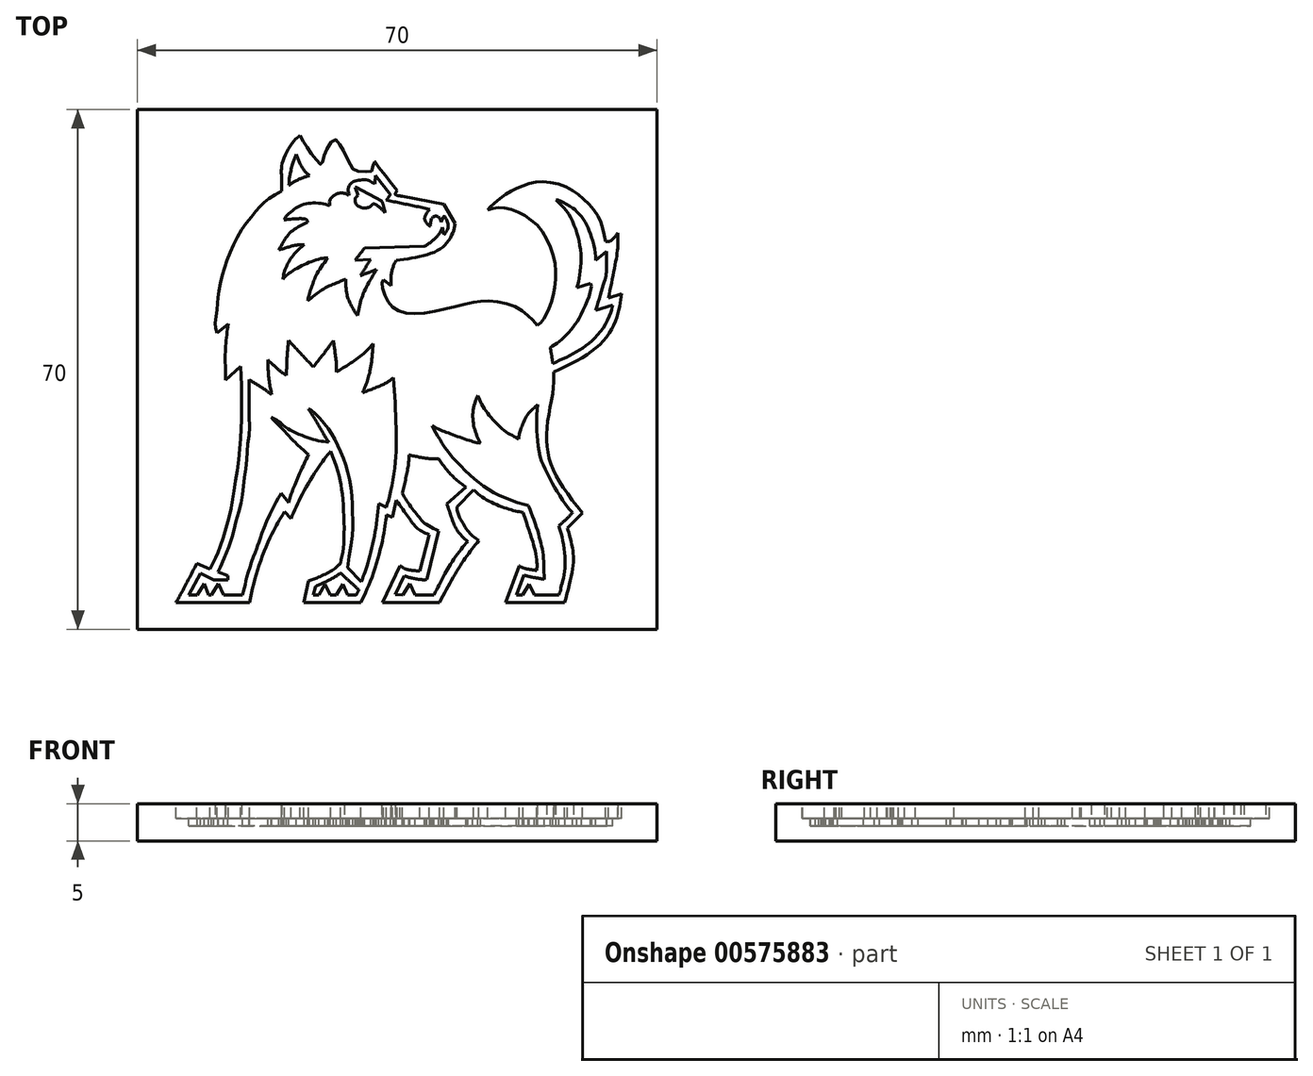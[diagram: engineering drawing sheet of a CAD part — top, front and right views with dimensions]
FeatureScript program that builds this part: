
annotation { "Feature Type Name" : "Feature", "Feature Type Description" : "" }
export const myFeature = defineFeature(function(context is Context, id is Id, definition is map)
    precondition{}
    {
        {
            var Q0;
            Q0=qCreatedBy(makeId("Top.planeOp"),FACE);
            var sketch = newSketch(context, id + "F0", { "sketchPlane" : qUnion([Q0])});
            skLineSegment(sketch, "E0.bottom", {"start": v(0, 0) * mm, "end": v(70, 0) * mm});
            skLineSegment(sketch, "E0.top", {"start": v(0, 70) * mm, "end": v(70, 70) * mm});
            skLineSegment(sketch, "E0.left", {"start": v(0, 0) * mm, "end": v(0, 70) * mm});
            skLineSegment(sketch, "E0.right", {"start": v(70, 0) * mm, "end": v(70, 70) * mm});
            skSolve(sketch);
        }
        {
            var Q0;
            Q0 = qSketchRegion(id + "F0", true);
            extrude(context, id + "F1", {"entities" : qUnion([Q0]), "depth" : 5 * mm, "offsetDistance" : 25 * mm});
        }
        {
            var Q0;
            Q0=makeQuery(id+"F1.opExtrude","CAP_FACE",FACE,{"disambiguationData":[OSD([sQuery(id+"F0.wireOp",EDGE,"E0.bottom"),sQuery(id+"F0.wireOp",EDGE,"E0.top"),sQuery(id+"F0.wireOp",EDGE,"E0.left"),sQuery(id+"F0.wireOp",EDGE,"E0.right")])],"isStart":false});
            var sketch = newSketch(context, id + "F2", { "sketchPlane" : qUnion([Q0])});
            skLineSegment(sketch, "E1", {"start": v(2.5, 2.5) * mm, "end": v(0, 2.5) * mm});
            skLineSegment(sketch, "E2", {"start": v(67.5, 67.5) * mm, "end": v(67.5, 70) * mm});
            skFitSpline(sketch, "E3", {"points": [v(21.94, 66.5) * mm, v(22.53, 65.47) * mm, v(23.24, 64.36) * mm, v(24.27, 63.03) * mm, v(24.75, 62.63) * mm, v(24.92, 62.83) * mm, v(25.12, 63.73) * mm, v(25.77, 65.15) * mm, v(26.63, 65.97) * mm, v(27.13, 65.54) * mm, v(27.88, 64.24) * mm, v(29.14, 61.88) * mm, v(29.98, 61.7) * mm, v(31.5, 61.67) * mm, v(31.61, 61.88) * mm, v(31.95, 63.03) * mm, v(32.14, 62.8) * mm, v(33.59, 60.92) * mm, v(35, 59.1) * mm], "startDerivative": vector(10.08, -18.23) * mm, "endDerivative": vector(16.66, -21.81) * mm});
            skFitSpline(sketch, "E4", {"points": [v(35, 59.1) * mm, v(34.77, 58.58) * mm, v(35.68, 58.34) * mm], "startDerivative": vector(-1, -1.38) * mm, "endDerivative": vector(2.24, -0.2) * mm});
            skFitSpline(sketch, "E5", {"points": [v(35.68, 58.34) * mm, v(41.28, 57.23) * mm], "startDerivative": vector(5.6, -1.11) * mm, "endDerivative": vector(5.6, -1.11) * mm});
            skFitSpline(sketch, "E6", {"points": [v(41.28, 57.23) * mm, v(42.8, 54.64) * mm], "startDerivative": vector(1.51, -2.6) * mm, "endDerivative": vector(1.51, -2.6) * mm});
            skFitSpline(sketch, "E7", {"points": [v(42.8, 54.64) * mm, v(42.56, 53.6) * mm, v(41.81, 52.2) * mm, v(40.47, 51.03) * mm, v(37.83, 50.17) * mm, v(34.89, 49.7) * mm], "startDerivative": vector(-1.1, -6.76) * mm, "endDerivative": vector(-11.91, -1.57) * mm});
            skFitSpline(sketch, "E8", {"points": [v(34.89, 49.7) * mm, v(34.47, 48.87) * mm, v(34.17, 47.56) * mm, v(34.2, 46.28) * mm], "startDerivative": vector(-1.48, -2.6) * mm, "endDerivative": vector(0.3, -3.62) * mm});
            skFitSpline(sketch, "E9", {"points": [v(34.2, 46.28) * mm, v(33.16, 47.08) * mm], "startDerivative": vector(-1.05, 0.8) * mm, "endDerivative": vector(-1.05, 0.8) * mm});
            skFitSpline(sketch, "E10", {"points": [v(33.16, 47.08) * mm, v(32.94, 46.66) * mm, v(33.34, 45) * mm, v(34.44, 43.36) * mm, v(36.65, 42.53) * mm, v(40.63, 42.94) * mm, v(44.7, 43.94) * mm, v(47.06, 44.24) * mm, v(50.35, 43.7) * mm, v(52.54, 42.35) * mm, v(53.84, 40.92) * mm], "startDerivative": vector(-6.38, -7.42) * mm, "endDerivative": vector(13.18, -16.1) * mm});
            skFitSpline(sketch, "E11", {"points": [v(53.84, 40.92) * mm, v(54.6, 41.6) * mm, v(55.27, 42.84) * mm, v(55.9, 44.58) * mm, v(56.34, 47.49) * mm, v(56.06, 50.23) * mm, v(54.6, 53.51) * mm, v(52.64, 55.43) * mm, v(50.35, 56.57) * mm, v(48.53, 56.8) * mm, v(47.19, 56.51) * mm], "startDerivative": vector(11.68, 8.6) * mm, "endDerivative": vector(-16.17, -4.46) * mm});
            skFitSpline(sketch, "E12", {"points": [v(47.19, 56.51) * mm, v(47.74, 57.1) * mm, v(49.46, 58.49) * mm, v(51.18, 59.46) * mm, v(53.06, 60.1) * mm, v(55.3, 60.25) * mm, v(58.13, 59.4) * mm, v(60, 58.07) * mm, v(61.73, 56.18) * mm, v(62.66, 54.16) * mm, v(63.05, 52.27) * mm], "startDerivative": vector(7.28, 8.52) * mm, "endDerivative": vector(3.26, -19.58) * mm});
            skFitSpline(sketch, "E13", {"points": [v(63.05, 52.27) * mm, v(63.65, 52.27) * mm, v(64.7, 53.35) * mm], "startDerivative": vector(1.5, -0.34) * mm, "endDerivative": vector(1.75, 2.31) * mm});
            skFitSpline(sketch, "E14", {"points": [v(64.7, 53.35) * mm, v(64.7, 51.32) * mm, v(63.43, 44.64) * mm], "startDerivative": vector(0.35, -4.94) * mm, "endDerivative": vector(-2.58, -11.82) * mm});
            skFitSpline(sketch, "E15", {"points": [v(63.43, 44.64) * mm, v(65.22, 45.2) * mm], "startDerivative": vector(1.79, 0.56) * mm, "endDerivative": vector(1.79, 0.56) * mm});
            skFitSpline(sketch, "E16", {"points": [v(65.22, 45.2) * mm, v(64.96, 43.49) * mm, v(64.13, 40.92) * mm, v(61.62, 37.75) * mm, v(56.08, 34.65) * mm], "startDerivative": vector(-1.16, -9.37) * mm, "endDerivative": vector(-18.65, -8.62) * mm});
            skFitSpline(sketch, "E17", {"points": [v(56.08, 34.65) * mm, v(56.08, 32.87) * mm, v(55.6, 29.96) * mm, v(55.14, 26.8) * mm, v(55.23, 24.22) * mm, v(55.84, 21.85) * mm, v(57.37, 19.08) * mm, v(59.93, 15.67) * mm], "startDerivative": vector(0.72, -14.91) * mm, "endDerivative": vector(15.62, -19.82) * mm});
            skFitSpline(sketch, "E18", {"points": [v(59.93, 15.67) * mm, v(57.93, 13.63) * mm], "startDerivative": vector(-2, -2.04) * mm, "endDerivative": vector(-2, -2.04) * mm});
            skFitSpline(sketch, "E19", {"points": [v(57.93, 13.63) * mm, v(58.26, 12.43) * mm, v(58.68, 10.46) * mm, v(58.61, 8.13) * mm, v(57.56, 3.57) * mm], "startDerivative": vector(1.74, -6.23) * mm, "endDerivative": vector(-3.71, -14.22) * mm});
            skFitSpline(sketch, "E20", {"points": [v(57.56, 3.57) * mm, v(49.62, 3.57) * mm], "startDerivative": vector(-7.94, 0) * mm, "endDerivative": vector(-7.94, 0) * mm});
            skFitSpline(sketch, "E21", {"points": [v(49.62, 3.57) * mm, v(51.43, 8.58) * mm], "startDerivative": vector(1.8, 5) * mm, "endDerivative": vector(1.8, 5) * mm});
            skFitSpline(sketch, "E22", {"points": [v(51.43, 8.58) * mm, v(52.01, 8.25) * mm, v(53.8, 7.92) * mm], "startDerivative": vector(1.3, -0.93) * mm, "endDerivative": vector(3.28, -0.42) * mm});
            skFitSpline(sketch, "E23", {"points": [v(53.8, 7.92) * mm, v(53.8, 9.35) * mm, v(53.21, 11.98) * mm, v(52.67, 13.6) * mm, v(51.94, 15.74) * mm], "startDerivative": vector(0.45, 6.08) * mm, "endDerivative": vector(-2.87, 8.51) * mm});
            skFitSpline(sketch, "E24", {"points": [v(51.94, 15.74) * mm, v(50.67, 16) * mm, v(48.8, 16.61) * mm, v(46.54, 17.76) * mm, v(45.32, 18.77) * mm], "startDerivative": vector(-5.8, 1.04) * mm, "endDerivative": vector(-4.65, 4.34) * mm});
            skFitSpline(sketch, "E25", {"points": [v(45.32, 18.77) * mm, v(43.04, 16.47) * mm], "startDerivative": vector(-2.28, -2.3) * mm, "endDerivative": vector(-2.28, -2.3) * mm});
            skFitSpline(sketch, "E26", {"points": [v(43.04, 16.47) * mm, v(43.23, 15.46) * mm, v(43.79, 14.38) * mm, v(44.78, 12.95) * mm, v(46, 11.96) * mm], "startDerivative": vector(0.53, -4.75) * mm, "endDerivative": vector(4.8, -3.28) * mm});
            skFitSpline(sketch, "E27", {"points": [v(46, 11.96) * mm, v(43.65, 8.81) * mm, v(40.7, 3.6) * mm], "startDerivative": vector(-5.23, -6.5) * mm, "endDerivative": vector(-5.37, -10.1) * mm});
            skFitSpline(sketch, "E28", {"points": [v(40.7, 3.6) * mm, v(33.04, 3.6) * mm], "startDerivative": vector(-7.66, 0) * mm, "endDerivative": vector(-7.66, 0) * mm});
            skFitSpline(sketch, "E29", {"points": [v(33.04, 3.6) * mm, v(35.41, 8.57) * mm], "startDerivative": vector(2.37, 4.98) * mm, "endDerivative": vector(2.37, 4.98) * mm});
            skFitSpline(sketch, "E30", {"points": [v(35.41, 8.57) * mm, v(36.16, 8.11) * mm, v(38.04, 7.86) * mm], "startDerivative": vector(1.6, -1.27) * mm, "endDerivative": vector(3.54, -0.23) * mm});
            skFitSpline(sketch, "E31", {"points": [v(38.04, 7.86) * mm, v(39.35, 12.73) * mm], "startDerivative": vector(1.3, 4.88) * mm, "endDerivative": vector(1.3, 4.88) * mm});
            skFitSpline(sketch, "E32", {"points": [v(39.35, 12.73) * mm, v(37.69, 13.62) * mm, v(36.78, 14.75) * mm, v(34.88, 17.36) * mm], "startDerivative": vector(-5.91, 2.6) * mm, "endDerivative": vector(-5.17, 6.96) * mm});
            skFitSpline(sketch, "E33", {"points": [v(34.88, 17.36) * mm, v(34.35, 15.07) * mm], "startDerivative": vector(-0.53, -2.3) * mm, "endDerivative": vector(-0.53, -2.3) * mm});
            skFitSpline(sketch, "E34", {"points": [v(34.35, 15.07) * mm, v(33.56, 15.42) * mm], "startDerivative": vector(-0.8, 0.36) * mm, "endDerivative": vector(-0.8, 0.36) * mm});
            skFitSpline(sketch, "E35", {"points": [v(33.56, 15.42) * mm, v(33.34, 13.76) * mm, v(32.7, 10.62) * mm, v(31.34, 6.32) * mm, v(30.09, 3.6) * mm], "startDerivative": vector(-0.98, -8.32) * mm, "endDerivative": vector(-5, -10.1) * mm});
            skFitSpline(sketch, "E36", {"points": [v(30.09, 3.6) * mm, v(22.41, 3.6) * mm], "startDerivative": vector(-7.67, 0) * mm, "endDerivative": vector(-7.67, 0) * mm});
            skFitSpline(sketch, "E37", {"points": [v(22.41, 3.6) * mm, v(23.08, 6.52) * mm], "startDerivative": vector(0.66, 2.92) * mm, "endDerivative": vector(0.66, 2.92) * mm});
            skFitSpline(sketch, "E38", {"points": [v(23.08, 6.52) * mm, v(24.52, 7.06) * mm, v(26.52, 8.13) * mm, v(27.35, 8.9) * mm], "startDerivative": vector(4.12, 1.43) * mm, "endDerivative": vector(2.47, 2.69) * mm});
            skFitSpline(sketch, "E39", {"points": [v(27.35, 8.9) * mm, v(27.72, 10.73) * mm, v(27.85, 13.89) * mm, v(27.64, 18) * mm, v(27.16, 20.72) * mm, v(26.06, 24) * mm], "startDerivative": vector(2.64, 10.97) * mm, "endDerivative": vector(-5.84, 15.89) * mm});
            skFitSpline(sketch, "E40", {"points": [v(26.06, 24) * mm, v(24.63, 22.16) * mm, v(22.18, 18.11) * mm, v(20.7, 14.9) * mm], "startDerivative": vector(-4.86, -5.86) * mm, "endDerivative": vector(-3.84, -9.06) * mm});
            skFitSpline(sketch, "E41", {"points": [v(20.7, 14.9) * mm, v(19.85, 15.86) * mm], "startDerivative": vector(-0.85, 0.97) * mm, "endDerivative": vector(-0.85, 0.97) * mm});
            skFitSpline(sketch, "E42", {"points": [v(19.85, 15.86) * mm, v(19, 14.48) * mm, v(18.31, 13.2) * mm, v(17.07, 10.41) * mm, v(15.88, 6.95) * mm, v(15.13, 3.6) * mm], "startDerivative": vector(-5.6, -8.96) * mm, "endDerivative": vector(-2.86, -14.46) * mm});
            skFitSpline(sketch, "E43", {"points": [v(15.13, 3.6) * mm, v(5.21, 3.6) * mm], "startDerivative": vector(-9.92, 0) * mm, "endDerivative": vector(-9.92, 0) * mm});
            skFitSpline(sketch, "E44", {"points": [v(5.21, 3.6) * mm, v(6.22, 5.4) * mm, v(8.02, 8.9) * mm], "startDerivative": vector(2.25, 3.92) * mm, "endDerivative": vector(3.3, 6.54) * mm});
            skFitSpline(sketch, "E45", {"points": [v(8.02, 8.9) * mm, v(9.78, 8.14) * mm], "startDerivative": vector(1.76, -0.75) * mm, "endDerivative": vector(1.76, -0.75) * mm});
            skFitSpline(sketch, "E46", {"points": [v(9.78, 8.14) * mm, v(10.57, 9.68) * mm, v(11.24, 11.34) * mm, v(12.48, 15.57) * mm, v(13.14, 19.24) * mm, v(13.8, 24.24) * mm, v(14.03, 28.47) * mm, v(14.06, 31.53) * mm, v(13.89, 35.42) * mm], "startDerivative": vector(9.35, 17.64) * mm, "endDerivative": vector(-1.76, 30.16) * mm});
            skFitSpline(sketch, "E47", {"points": [v(13.89, 35.42) * mm, v(11.87, 33.56) * mm], "startDerivative": vector(-2.02, -1.86) * mm, "endDerivative": vector(-2.02, -1.86) * mm});
            skFitSpline(sketch, "E48", {"points": [v(11.87, 33.56) * mm, v(11.87, 34.73) * mm, v(11.87, 37.75) * mm, v(12.27, 41.13) * mm], "startDerivative": vector(0.05, 4.42) * mm, "endDerivative": vector(1.28, 8.4) * mm});
            skFitSpline(sketch, "E49", {"points": [v(12.27, 41.13) * mm, v(10.75, 39.9) * mm], "startDerivative": vector(-1.52, -1.22) * mm, "endDerivative": vector(-1.52, -1.22) * mm});
            skFitSpline(sketch, "E50", {"points": [v(10.75, 39.9) * mm, v(10.5, 41.13) * mm, v(10.75, 43.28) * mm, v(10.92, 45.16) * mm, v(11.53, 48.02) * mm, v(12.63, 51.08) * mm, v(14.32, 54.2) * mm, v(16.1, 56.46) * mm, v(17.33, 57.7) * mm, v(19.42, 59.06) * mm], "startDerivative": vector(-4.25, 13.95) * mm, "endDerivative": vector(20.21, 12) * mm});
            skFitSpline(sketch, "E51", {"points": [v(19.42, 59.06) * mm, v(19.42, 60.87) * mm, v(19.42, 62) * mm, v(19.85, 63.74) * mm, v(21.14, 65.83) * mm, v(21.94, 66.5) * mm], "startDerivative": vector(0.09, 9.13) * mm, "endDerivative": vector(4.8, 3.22) * mm});
            skSolve(sketch);
        }
        {
            var Q0;
            Q0 = qSketchRegion(id + "F2", true);
            extrude(context, id + "F3", {"entities" : qUnion([Q0]), "operationType" : NewBodyOperationType.REMOVE, "oppositeDirection" : true, "depth" : 2 * mm, "offsetDistance" : 25 * mm});
        }
        {
            var Q0;
            Q0=makeQuery(id+"F3.boolean.opBoolean","COPY",FACE,{"derivedFrom":makeQuery(id+"F3.opExtrude","CAP_FACE",FACE,{"disambiguationData":[OSD([sQuery(id+"F2.wireOp",EDGE,"E3"),sQuery(id+"F2.wireOp",EDGE,"E4"),sQuery(id+"F2.wireOp",EDGE,"E5"),sQuery(id+"F2.wireOp",EDGE,"E6"),sQuery(id+"F2.wireOp",EDGE,"E7"),sQuery(id+"F2.wireOp",EDGE,"E8"),sQuery(id+"F2.wireOp",EDGE,"E9"),sQuery(id+"F2.wireOp",EDGE,"E10"),sQuery(id+"F2.wireOp",EDGE,"E11"),sQuery(id+"F2.wireOp",EDGE,"E12"),sQuery(id+"F2.wireOp",EDGE,"E13"),sQuery(id+"F2.wireOp",EDGE,"E14"),sQuery(id+"F2.wireOp",EDGE,"E15"),sQuery(id+"F2.wireOp",EDGE,"E16"),sQuery(id+"F2.wireOp",EDGE,"E17"),sQuery(id+"F2.wireOp",EDGE,"E18"),sQuery(id+"F2.wireOp",EDGE,"E19"),sQuery(id+"F2.wireOp",EDGE,"E20"),sQuery(id+"F2.wireOp",EDGE,"E21"),sQuery(id+"F2.wireOp",EDGE,"E22"),sQuery(id+"F2.wireOp",EDGE,"E23"),sQuery(id+"F2.wireOp",EDGE,"E24"),sQuery(id+"F2.wireOp",EDGE,"E25"),sQuery(id+"F2.wireOp",EDGE,"E26"),sQuery(id+"F2.wireOp",EDGE,"E27"),sQuery(id+"F2.wireOp",EDGE,"E28"),sQuery(id+"F2.wireOp",EDGE,"E29"),sQuery(id+"F2.wireOp",EDGE,"E30"),sQuery(id+"F2.wireOp",EDGE,"E31"),sQuery(id+"F2.wireOp",EDGE,"E32"),sQuery(id+"F2.wireOp",EDGE,"E33"),sQuery(id+"F2.wireOp",EDGE,"E34"),sQuery(id+"F2.wireOp",EDGE,"E35"),sQuery(id+"F2.wireOp",EDGE,"E36"),sQuery(id+"F2.wireOp",EDGE,"E37"),sQuery(id+"F2.wireOp",EDGE,"E38"),sQuery(id+"F2.wireOp",EDGE,"E39"),sQuery(id+"F2.wireOp",EDGE,"E40"),sQuery(id+"F2.wireOp",EDGE,"E41"),sQuery(id+"F2.wireOp",EDGE,"E42"),sQuery(id+"F2.wireOp",EDGE,"E43"),sQuery(id+"F2.wireOp",EDGE,"E44"),sQuery(id+"F2.wireOp",EDGE,"E45"),sQuery(id+"F2.wireOp",EDGE,"E46"),sQuery(id+"F2.wireOp",EDGE,"E47"),sQuery(id+"F2.wireOp",EDGE,"E48"),sQuery(id+"F2.wireOp",EDGE,"E49"),sQuery(id+"F2.wireOp",EDGE,"E50"),sQuery(id+"F2.wireOp",EDGE,"E51")])],"isStart":false})});
            var sketch = newSketch(context, id + "F4", { "sketchPlane" : qUnion([Q0])});
            skFitSpline(sketch, "E52", {"points": [v(20.42, 59.78) * mm, v(21, 60.21) * mm, v(22.13, 60.77) * mm, v(23.2, 61.12) * mm], "startDerivative": vector(1.84, 1.52) * mm, "endDerivative": vector(3, 0.87) * mm});
            skFitSpline(sketch, "E53", {"points": [v(23.2, 61.12) * mm, v(22.68, 61.57) * mm, v(22, 62.57) * mm, v(21.4, 63.96) * mm], "startDerivative": vector(-1.98, 1.5) * mm, "endDerivative": vector(-1.43, 3.68) * mm});
            skFitSpline(sketch, "E54", {"points": [v(21.4, 63.96) * mm, v(21.11, 63.27) * mm, v(20.84, 62.48) * mm, v(20.58, 61.29) * mm, v(20.48, 60.76) * mm, v(20.42, 59.78) * mm], "startDerivative": vector(-1.6, -3.7) * mm, "endDerivative": vector(-0.22, -5.05) * mm});
            skFitSpline(sketch, "E55", {"points": [v(32.02, 60.2) * mm, v(32.09, 61.13) * mm], "startDerivative": vector(0.07, 0.92) * mm, "endDerivative": vector(0.07, 0.92) * mm});
            skFitSpline(sketch, "E56", {"points": [v(32.09, 61.13) * mm, v(34.08, 58.55) * mm], "startDerivative": vector(2, -2.58) * mm, "endDerivative": vector(2, -2.58) * mm});
            skFitSpline(sketch, "E57", {"points": [v(34.08, 58.55) * mm, v(33.57, 57.82) * mm], "startDerivative": vector(-0.43, -0.6) * mm, "endDerivative": vector(-0.43, -0.6) * mm});
            skFitSpline(sketch, "E58", {"points": [v(33.57, 57.82) * mm, v(39.38, 56.58) * mm], "startDerivative": vector(5.8, -1.3) * mm, "endDerivative": vector(5.8, -1.3) * mm});
            skFitSpline(sketch, "E59", {"points": [v(39.38, 56.58) * mm, v(39, 56.12) * mm, v(38.73, 55.54) * mm, v(38.75, 55.1) * mm, v(39.04, 54.64) * mm, v(39.48, 54.3) * mm], "startDerivative": vector(-1.81, -2.11) * mm, "endDerivative": vector(2.33, -1.56) * mm});
            skFitSpline(sketch, "E60", {"points": [v(39.48, 54.3) * mm, v(39.48, 54.74) * mm, v(39.66, 55.33) * mm, v(40, 55.61) * mm, v(40.45, 55.62) * mm, v(40.8, 55.25) * mm, v(40.93, 54.84) * mm], "startDerivative": vector(-0.26, 2.55) * mm, "endDerivative": vector(0.96, -2.36) * mm});
            skFitSpline(sketch, "E61", {"points": [v(40.93, 54.84) * mm, v(41.15, 55.34) * mm, v(41.32, 55.64) * mm, v(41.54, 55.38) * mm, v(41.87, 54.52) * mm, v(41.74, 53.8) * mm, v(41.3, 53.16) * mm], "startDerivative": vector(1.57, 2.35) * mm, "endDerivative": vector(-2.76, -2.4) * mm});
            skFitSpline(sketch, "E62", {"points": [v(41.3, 53.16) * mm, v(41.1, 54.16) * mm], "startDerivative": vector(-0.37, 0.86) * mm, "endDerivative": vector(-0.2, 0.95) * mm});
            skFitSpline(sketch, "E63", {"points": [v(41.1, 54.16) * mm, v(40.83, 53.57) * mm, v(40.42, 52.97) * mm, v(39.63, 52.23) * mm, v(38.71, 51.6) * mm], "startDerivative": vector(-1.2, -2.77) * mm, "endDerivative": vector(-3.3, -2.09) * mm});
            skFitSpline(sketch, "E64", {"points": [v(38.71, 51.6) * mm, v(30.6, 51.34) * mm], "startDerivative": vector(-8.1, -0.27) * mm, "endDerivative": vector(-8.1, -0.27) * mm});
            skFitSpline(sketch, "E65", {"points": [v(30.6, 51.34) * mm, v(29.35, 49.72) * mm], "startDerivative": vector(-1.23, -1.52) * mm, "endDerivative": vector(-1.23, -1.52) * mm});
            skFitSpline(sketch, "E66", {"points": [v(29.35, 49.72) * mm, v(31.42, 49.84) * mm], "startDerivative": vector(2.07, 0.12) * mm, "endDerivative": vector(2.07, 0.12) * mm});
            skFitSpline(sketch, "E67", {"points": [v(31.42, 49.84) * mm, v(30.08, 47.65) * mm], "startDerivative": vector(-1.36, -2.13) * mm, "endDerivative": vector(-1.36, -2.13) * mm});
            skFitSpline(sketch, "E68", {"points": [v(30.08, 47.65) * mm, v(32.24, 48.47) * mm], "startDerivative": vector(2.18, 0.76) * mm, "endDerivative": vector(2.18, 0.76) * mm});
            skFitSpline(sketch, "E69", {"points": [v(32.24, 48.47) * mm, v(31.7, 47.6) * mm, v(30.77, 45.9) * mm, v(30.04, 44.04) * mm, v(29.66, 42.28) * mm], "startDerivative": vector(-2.49, -4.09) * mm, "endDerivative": vector(-1.2, -6.78) * mm});
            skFitSpline(sketch, "E70", {"points": [v(29.66, 42.28) * mm, v(29.23, 42.9) * mm, v(28.67, 43.97) * mm, v(28.27, 44.94) * mm, v(28.05, 47.16) * mm], "startDerivative": vector(-2.16, 2.9) * mm, "endDerivative": vector(-0.37, 7.46) * mm});
            skFitSpline(sketch, "E71", {"points": [v(28.05, 47.16) * mm, v(27.03, 46.74) * mm, v(25.14, 45.88) * mm, v(22.95, 44.23) * mm], "startDerivative": vector(-3.72, -1.57) * mm, "endDerivative": vector(-5.39, -4.54) * mm});
            skFitSpline(sketch, "E72", {"points": [v(22.95, 44.23) * mm, v(23.1, 44.94) * mm, v(23.57, 46.37) * mm, v(24.14, 47.75) * mm, v(25.66, 50.04) * mm], "startDerivative": vector(0.56, 3.76) * mm, "endDerivative": vector(5.43, 7.2) * mm});
            skFitSpline(sketch, "E73", {"points": [v(25.66, 50.04) * mm, v(24.96, 49.98) * mm, v(23.62, 49.61) * mm, v(22.16, 48.98) * mm, v(20.78, 48.18) * mm, v(20.02, 47.6) * mm, v(19.66, 47.18) * mm], "startDerivative": vector(-4.81, -0.15) * mm, "endDerivative": vector(-2.73, -3.54) * mm});
            skFitSpline(sketch, "E74", {"points": [v(19.66, 47.18) * mm, v(19.71, 47.73) * mm, v(20.22, 49.18) * mm, v(21.33, 50.77) * mm, v(22.47, 51.8) * mm], "startDerivative": vector(0.14, 3) * mm, "endDerivative": vector(4.29, 3.51) * mm});
            skFitSpline(sketch, "E75", {"points": [v(22.47, 51.8) * mm, v(21.76, 51.8) * mm, v(20.58, 51.56) * mm, v(19.08, 51.08) * mm], "startDerivative": vector(-2.55, 0.13) * mm, "endDerivative": vector(-3.88, -1.3) * mm});
            skFitSpline(sketch, "E76", {"points": [v(19.08, 51.08) * mm, v(19.46, 51.8) * mm, v(20.63, 53.44) * mm, v(22.93, 54.87) * mm], "startDerivative": vector(1.48, 2.78) * mm, "endDerivative": vector(6.07, 2.96) * mm});
            skFitSpline(sketch, "E77", {"points": [v(22.93, 54.87) * mm, v(22.75, 55.2) * mm, v(19.77, 55.15) * mm], "startDerivative": vector(-0.23, 1.45) * mm, "endDerivative": vector(-5.3, -0.56) * mm});
            skFitSpline(sketch, "E78", {"points": [v(19.77, 55.15) * mm, v(20.24, 55.85) * mm, v(21.15, 56.6) * mm, v(22.06, 57.1) * mm, v(23.29, 57.4) * mm, v(24.67, 57.38) * mm, v(25.94, 57.04) * mm], "startDerivative": vector(2.82, 5) * mm, "endDerivative": vector(7.06, -2.27) * mm});
            skFitSpline(sketch, "E79", {"points": [v(25.94, 57.04) * mm, v(25.94, 57.84) * mm, v(26.56, 58.46) * mm, v(27.23, 58.75) * mm, v(28.05, 58.69) * mm, v(28.43, 58.43) * mm], "startDerivative": vector(-0.71, 4) * mm, "endDerivative": vector(2.05, -1.83) * mm});
            skFitSpline(sketch, "E80", {"points": [v(28.43, 58.43) * mm, v(28.6, 58.7) * mm], "startDerivative": vector(0.16, 0.27) * mm, "endDerivative": vector(0.16, 0.27) * mm});
            skFitSpline(sketch, "E81", {"points": [v(28.6, 58.7) * mm, v(28.43, 58.9) * mm, v(28.43, 59.43) * mm, v(28.73, 59.98) * mm, v(29.13, 60.3) * mm, v(29.93, 60.5) * mm, v(30.84, 60.56) * mm, v(31.48, 60.28) * mm, v(31.99, 60.01) * mm], "startDerivative": vector(-2.23, 2.09) * mm, "endDerivative": vector(4.05, -2.09) * mm});
            skFitSpline(sketch, "E82", {"points": [v(31.99, 60.01) * mm, v(32.02, 60.2) * mm], "startDerivative": vector(0.03, 0.2) * mm, "endDerivative": vector(0.03, 0.2) * mm});
            skFitSpline(sketch, "E83", {"points": [v(29.34, 59.53) * mm, v(29.7, 58.46) * mm], "startDerivative": vector(0.36, -1.08) * mm, "endDerivative": vector(0.36, -1.08) * mm});
            skFitSpline(sketch, "E84", {"points": [v(29.7, 58.46) * mm, v(29.44, 58.18) * mm, v(29.34, 58) * mm, v(29.32, 57.75) * mm], "startDerivative": vector(-0.58, -0.8) * mm, "endDerivative": vector(0.15, -0.78) * mm});
            skFitSpline(sketch, "E85", {"points": [v(29.32, 57.75) * mm, v(29.38, 57.45) * mm, v(29.55, 57.18) * mm, v(30.09, 56.85) * mm, v(30.9, 56.77) * mm, v(31.35, 56.92) * mm, v(31.75, 57.34) * mm], "startDerivative": vector(0.34, -2.3) * mm, "endDerivative": vector(2.19, 2.73) * mm});
            skFitSpline(sketch, "E86", {"points": [v(31.75, 57.34) * mm, v(32.01, 57.26) * mm, v(32.43, 57) * mm, v(33.19, 56.3) * mm, v(33.35, 56.1) * mm], "startDerivative": vector(1.33, -0.35) * mm, "endDerivative": vector(0.64, -0.9) * mm});
            skFitSpline(sketch, "E87", {"points": [v(33.35, 56.1) * mm, v(33.35, 56.33) * mm, v(33.24, 56.73) * mm, v(33.1, 57.26) * mm, v(32.92, 57.68) * mm], "startDerivative": vector(0.1, 1.16) * mm, "endDerivative": vector(-0.7, 1.51) * mm});
            skFitSpline(sketch, "E88", {"points": [v(32.92, 57.68) * mm, v(29.5, 59.55) * mm], "startDerivative": vector(-3.42, 1.87) * mm, "endDerivative": vector(-3.42, 1.87) * mm});
            skFitSpline(sketch, "E89", {"points": [v(29.5, 59.55) * mm, v(29.34, 59.53) * mm], "startDerivative": vector(-0.16, -0.01) * mm, "endDerivative": vector(-0.16, -0.01) * mm});
            skFitSpline(sketch, "E90", {"points": [v(55.63, 37.95) * mm, v(56.82, 38.75) * mm, v(58.35, 40.27) * mm, v(59.83, 42.5) * mm, v(61.15, 46.12) * mm, v(61.03, 46.6) * mm], "startDerivative": vector(6.82, 4.05) * mm, "endDerivative": vector(-1.98, 3.38) * mm});
            skFitSpline(sketch, "E91", {"points": [v(61.03, 46.6) * mm, v(59.18, 46) * mm], "startDerivative": vector(-1.84, -0.59) * mm, "endDerivative": vector(-1.84, -0.59) * mm});
            skFitSpline(sketch, "E92", {"points": [v(59.18, 46) * mm, v(59.44, 46.78) * mm, v(59.58, 47.6) * mm, v(59.7, 48.8) * mm, v(59.76, 50.16) * mm, v(59.62, 51.67) * mm, v(59.34, 52.95) * mm, v(58.94, 54.15) * mm, v(58.38, 55.4) * mm, v(57.75, 56.44) * mm, v(56.42, 57.84) * mm], "startDerivative": vector(3.59, 9.58) * mm, "endDerivative": vector(-11.95, 11.67) * mm});
            skFitSpline(sketch, "E93", {"points": [v(56.42, 57.84) * mm, v(56.82, 57.75) * mm, v(58.17, 57.05) * mm, v(59.05, 56.4) * mm, v(59.91, 55.47) * mm, v(60.6, 54.3) * mm, v(61.03, 53.23) * mm, v(61.53, 51.5) * mm, v(61.75, 49.67) * mm], "startDerivative": vector(4.68, -0.62) * mm, "endDerivative": vector(0.96, -12.04) * mm});
            skFitSpline(sketch, "E94", {"points": [v(61.75, 49.67) * mm, v(63.2, 50.9) * mm], "startDerivative": vector(1.44, 1.23) * mm, "endDerivative": vector(1.44, 1.23) * mm});
            skFitSpline(sketch, "E95", {"points": [v(63.2, 50.9) * mm, v(63.2, 49.9) * mm, v(63.2, 48.16) * mm, v(62.93, 46.92) * mm, v(61.75, 43) * mm], "startDerivative": vector(-0.06, -4.95) * mm, "endDerivative": vector(-3.7, -12.29) * mm});
            skFitSpline(sketch, "E96", {"points": [v(61.75, 43) * mm, v(64, 43.7) * mm], "startDerivative": vector(2.25, 0.7) * mm, "endDerivative": vector(2.25, 0.7) * mm});
            skFitSpline(sketch, "E97", {"points": [v(64, 43.7) * mm, v(63.8, 42.82) * mm, v(62.75, 40.62) * mm, v(61.1, 38.73) * mm, v(59.5, 37.57) * mm, v(57.69, 36.6) * mm, v(55.96, 35.78) * mm], "startDerivative": vector(-1.24, -6.72) * mm, "endDerivative": vector(-10.29, -4.83) * mm});
            skFitSpline(sketch, "E98", {"points": [v(55.96, 35.78) * mm, v(55.83, 36.7) * mm, v(55.63, 37.95) * mm], "startDerivative": vector(-0.25, 1.9) * mm, "endDerivative": vector(-0.41, 2.41) * mm});
            skFitSpline(sketch, "E99", {"points": [v(6.93, 4.65) * mm, v(8.06, 4.65) * mm], "startDerivative": vector(1.13, 0) * mm, "endDerivative": vector(1.13, 0) * mm});
            skFitSpline(sketch, "E100", {"points": [v(8.06, 4.65) * mm, v(9, 6.13) * mm], "startDerivative": vector(0.95, 1.48) * mm, "endDerivative": vector(0.95, 1.48) * mm});
            skFitSpline(sketch, "E101", {"points": [v(9, 6.13) * mm, v(9.6, 4.65) * mm], "startDerivative": vector(0.6, -1.48) * mm, "endDerivative": vector(0.6, -1.48) * mm});
            skFitSpline(sketch, "E102", {"points": [v(9.6, 4.65) * mm, v(10, 4.65) * mm], "startDerivative": vector(0.4, 0) * mm, "endDerivative": vector(0.4, 0) * mm});
            skFitSpline(sketch, "E103", {"points": [v(10, 4.65) * mm, v(10.92, 6.13) * mm], "startDerivative": vector(0.91, 1.48) * mm, "endDerivative": vector(0.91, 1.48) * mm});
            skFitSpline(sketch, "E104", {"points": [v(10.92, 6.13) * mm, v(11.65, 4.65) * mm], "startDerivative": vector(0.73, -1.48) * mm, "endDerivative": vector(0.73, -1.48) * mm});
            skFitSpline(sketch, "E105", {"points": [v(11.65, 4.65) * mm, v(14.16, 4.65) * mm], "startDerivative": vector(2.5, 0) * mm, "endDerivative": vector(2.5, 0) * mm});
            skFitSpline(sketch, "E106", {"points": [v(14.16, 4.65) * mm, v(14.5, 5.9) * mm, v(14.86, 7.37) * mm, v(15.79, 10.13) * mm, v(16.28, 11.46) * mm, v(17.1, 13.77) * mm, v(19.04, 17.74) * mm, v(19.4, 18.32) * mm], "startDerivative": vector(3.01, 10.8) * mm, "endDerivative": vector(3.39, 4.89) * mm});
            skFitSpline(sketch, "E107", {"points": [v(19.4, 18.32) * mm, v(20.37, 17.09) * mm], "startDerivative": vector(0.96, -1.23) * mm, "endDerivative": vector(0.96, -1.23) * mm});
            skFitSpline(sketch, "E108", {"points": [v(20.37, 17.09) * mm, v(20.7, 18.15) * mm, v(21.14, 19.27) * mm, v(22.08, 21.46) * mm, v(23.06, 23.54) * mm], "startDerivative": vector(1.6, 5.36) * mm, "endDerivative": vector(3.33, 6.9) * mm});
            skFitSpline(sketch, "E109", {"points": [v(23.06, 23.54) * mm, v(21.35, 25.08) * mm, v(19.92, 26.6) * mm, v(18.02, 28.54) * mm], "startDerivative": vector(-5.35, 4.64) * mm, "endDerivative": vector(-5.31, 5.37) * mm});
            skFitSpline(sketch, "E110", {"points": [v(18.02, 28.54) * mm, v(18.93, 28.07) * mm, v(20.37, 26.97) * mm, v(22.41, 26.01) * mm, v(24.26, 25.43) * mm, v(25.79, 25.21) * mm], "startDerivative": vector(7.85, -2.88) * mm, "endDerivative": vector(7.78, -0.78) * mm});
            skFitSpline(sketch, "E111", {"points": [v(25.79, 25.21) * mm, v(25.34, 25.91) * mm, v(24.42, 27.49) * mm, v(23.06, 29.68) * mm], "startDerivative": vector(-1.78, 2.66) * mm, "endDerivative": vector(-3.41, 5.36) * mm});
            skFitSpline(sketch, "E112", {"points": [v(23.06, 29.68) * mm, v(23.44, 29.52) * mm, v(24.5, 28.54) * mm, v(25.79, 26.96) * mm, v(26.7, 25.4) * mm, v(27.56, 23.54) * mm, v(28.26, 21.4) * mm, v(28.8, 18.69) * mm, v(28.98, 15.59) * mm, v(28.98, 13.1) * mm, v(28.3, 8.3) * mm], "startDerivative": vector(8.06, -2.2) * mm, "endDerivative": vector(-5.83, -35.14) * mm});
            skFitSpline(sketch, "E113", {"points": [v(28.3, 8.3) * mm, v(30.18, 6.4) * mm], "startDerivative": vector(1.88, -1.9) * mm, "endDerivative": vector(1.88, -1.9) * mm});
            skFitSpline(sketch, "E114", {"points": [v(30.18, 6.4) * mm, v(30.66, 7.7) * mm, v(31.76, 11.72) * mm, v(32.54, 16.93) * mm], "startDerivative": vector(2.01, 5.24) * mm, "endDerivative": vector(1.45, 12.58) * mm});
            skFitSpline(sketch, "E115", {"points": [v(32.54, 16.93) * mm, v(33.54, 16.46) * mm], "startDerivative": vector(1, -0.47) * mm, "endDerivative": vector(1, -0.47) * mm});
            skFitSpline(sketch, "E116", {"points": [v(33.54, 16.46) * mm, v(34.02, 18.1) * mm, v(34.69, 21.75) * mm, v(34.87, 25.21) * mm, v(34.79, 29.46) * mm, v(34.47, 33.86) * mm], "startDerivative": vector(3.26, 10.27) * mm, "endDerivative": vector(-1.63, 19.31) * mm});
            skFitSpline(sketch, "E117", {"points": [v(34.47, 33.86) * mm, v(33.36, 33.11) * mm, v(30.36, 31.89) * mm], "startDerivative": vector(-2.42, -1.9) * mm, "endDerivative": vector(-5.57, -2.04) * mm});
            skFitSpline(sketch, "E118", {"points": [v(30.36, 31.89) * mm, v(30.95, 33.37) * mm, v(31.45, 35.34) * mm, v(31.78, 38.48) * mm], "startDerivative": vector(2.2, 5.1) * mm, "endDerivative": vector(0.68, 8.33) * mm});
            skFitSpline(sketch, "E119", {"points": [v(31.78, 38.48) * mm, v(30.86, 37.48) * mm, v(28.68, 35.82) * mm, v(26.79, 34.65) * mm], "startDerivative": vector(-2.9, -3.52) * mm, "endDerivative": vector(-5.27, -3.08) * mm});
            skFitSpline(sketch, "E120", {"points": [v(26.79, 34.65) * mm, v(26.79, 36.02) * mm, v(26.55, 37.87) * mm, v(26.43, 38.92) * mm], "startDerivative": vector(0.17, 3.9) * mm, "endDerivative": vector(-0.32, 3.31) * mm});
            skFitSpline(sketch, "E121", {"points": [v(26.43, 38.92) * mm, v(25.54, 37.7) * mm, v(23.72, 35.34) * mm], "startDerivative": vector(-1.93, -2.71) * mm, "endDerivative": vector(-3.4, -4.35) * mm});
            skFitSpline(sketch, "E122", {"points": [v(23.72, 35.34) * mm, v(22.2, 36.92) * mm, v(20.37, 38.92) * mm], "startDerivative": vector(-3.15, 3.23) * mm, "endDerivative": vector(-3.55, 3.91) * mm});
            skFitSpline(sketch, "E123", {"points": [v(20.37, 38.92) * mm, v(20.2, 37.18) * mm, v(20.09, 34.2) * mm], "startDerivative": vector(-0.41, -3.74) * mm, "endDerivative": vector(-0.16, -5.62) * mm});
            skFitSpline(sketch, "E124", {"points": [v(20.09, 34.2) * mm, v(19.4, 34.65) * mm, v(17.62, 36.27) * mm], "startDerivative": vector(-1.67, 0.99) * mm, "endDerivative": vector(-3.14, 2.98) * mm});
            skFitSpline(sketch, "E125", {"points": [v(17.62, 36.27) * mm, v(17.62, 35.37) * mm, v(17.74, 33.6) * mm, v(18.1, 31.62) * mm], "startDerivative": vector(-0.04, -3.17) * mm, "endDerivative": vector(1.02, -4.83) * mm});
            skFitSpline(sketch, "E126", {"points": [v(18.1, 31.62) * mm, v(17.62, 31.96) * mm, v(16.48, 32.74) * mm, v(15.07, 33.6) * mm], "startDerivative": vector(-1.86, 0.63) * mm, "endDerivative": vector(-3.5, 2.03) * mm});
            skFitSpline(sketch, "E127", {"points": [v(15.07, 33.6) * mm, v(15.07, 32.71) * mm, v(15.07, 30.9) * mm, v(15.07, 29.2) * mm, v(15.07, 26.58) * mm, v(14.86, 24.63) * mm, v(14.72, 22.74) * mm, v(14.43, 20.45) * mm, v(14.2, 18.37) * mm, v(13.76, 16.19) * mm, v(13.09, 13.69) * mm, v(12.6, 11.89) * mm, v(11.26, 8.5) * mm, v(10.85, 7.75) * mm], "startDerivative": vector(-0.01, -15.46) * mm, "endDerivative": vector(-6.82, -10.97) * mm});
            skFitSpline(sketch, "E128", {"points": [v(10.85, 7.75) * mm, v(12.2, 7.2) * mm], "startDerivative": vector(1.34, -0.54) * mm, "endDerivative": vector(1.34, -0.54) * mm});
            skFitSpline(sketch, "E129", {"points": [v(12.2, 7.2) * mm, v(12.2, 6.63) * mm], "startDerivative": vector(0, -0.57) * mm, "endDerivative": vector(0, -0.57) * mm});
            skFitSpline(sketch, "E130", {"points": [v(12.2, 6.63) * mm, v(10.3, 6.63) * mm], "startDerivative": vector(-1.9, 0) * mm, "endDerivative": vector(-1.9, 0) * mm});
            skFitSpline(sketch, "E131", {"points": [v(10.3, 6.63) * mm, v(8.5, 7.51) * mm], "startDerivative": vector(-1.79, 0.88) * mm, "endDerivative": vector(-1.79, 0.88) * mm});
            skFitSpline(sketch, "E132", {"points": [v(8.5, 7.51) * mm, v(6.93, 4.65) * mm], "startDerivative": vector(-1.57, -2.87) * mm, "endDerivative": vector(-1.57, -2.87) * mm});
            skFitSpline(sketch, "E133", {"points": [v(23.72, 4.62) * mm, v(24.48, 4.6) * mm], "startDerivative": vector(0.76, 0) * mm, "endDerivative": vector(0.76, 0) * mm});
            skFitSpline(sketch, "E134", {"points": [v(24.48, 4.6) * mm, v(25.32, 6.08) * mm], "startDerivative": vector(0.84, 1.47) * mm, "endDerivative": vector(0.84, 1.47) * mm});
            skFitSpline(sketch, "E135", {"points": [v(25.32, 6.08) * mm, v(25.98, 4.6) * mm], "startDerivative": vector(0.66, -1.47) * mm, "endDerivative": vector(0.66, -1.47) * mm});
            skFitSpline(sketch, "E136", {"points": [v(25.98, 4.6) * mm, v(26.83, 4.6) * mm], "startDerivative": vector(0.85, 0) * mm, "endDerivative": vector(0.85, 0) * mm});
            skFitSpline(sketch, "E137", {"points": [v(26.83, 4.6) * mm, v(27.68, 6.08) * mm], "startDerivative": vector(0.85, 1.47) * mm, "endDerivative": vector(0.85, 1.47) * mm});
            skFitSpline(sketch, "E138", {"points": [v(27.68, 6.08) * mm, v(28.3, 4.6) * mm], "startDerivative": vector(0.63, -1.47) * mm, "endDerivative": vector(0.63, -1.47) * mm});
            skFitSpline(sketch, "E139", {"points": [v(28.3, 4.6) * mm, v(29.48, 4.6) * mm], "startDerivative": vector(1.18, 0) * mm, "endDerivative": vector(1.18, 0) * mm});
            skFitSpline(sketch, "E140", {"points": [v(29.48, 4.6) * mm, v(29.84, 5.3) * mm], "startDerivative": vector(0.34, 0.61) * mm, "endDerivative": vector(0.34, 0.61) * mm});
            skFitSpline(sketch, "E141", {"points": [v(29.84, 5.3) * mm, v(27.4, 7.56) * mm], "startDerivative": vector(-2.43, 2.34) * mm, "endDerivative": vector(-2.43, 2.34) * mm});
            skFitSpline(sketch, "E142", {"points": [v(27.4, 7.56) * mm, v(27.04, 7.33) * mm, v(26.25, 6.85) * mm, v(25.25, 6.35) * mm, v(24, 5.77) * mm], "startDerivative": vector(-1.85, -1.22) * mm, "endDerivative": vector(-4.2, -1.92) * mm});
            skFitSpline(sketch, "E143", {"points": [v(24, 5.77) * mm, v(23.72, 4.62) * mm], "startDerivative": vector(-0.29, -1.16) * mm, "endDerivative": vector(-0.29, -1.16) * mm});
            skFitSpline(sketch, "E144", {"points": [v(34.73, 4.66) * mm, v(35.77, 4.63) * mm], "startDerivative": vector(1.05, -0.03) * mm, "endDerivative": vector(1.05, -0.03) * mm});
            skFitSpline(sketch, "E145", {"points": [v(35.77, 4.63) * mm, v(36.74, 6.1) * mm], "startDerivative": vector(0.96, 1.48) * mm, "endDerivative": vector(0.96, 1.48) * mm});
            skFitSpline(sketch, "E146", {"points": [v(36.74, 6.1) * mm, v(37.43, 4.63) * mm], "startDerivative": vector(0.7, -1.48) * mm, "endDerivative": vector(0.7, -1.48) * mm});
            skFitSpline(sketch, "E147", {"points": [v(37.43, 4.63) * mm, v(39.94, 4.63) * mm], "startDerivative": vector(2.5, 0) * mm, "endDerivative": vector(2.5, 0) * mm});
            skFitSpline(sketch, "E148", {"points": [v(39.94, 4.63) * mm, v(40.37, 5.44) * mm, v(41.36, 7.31) * mm, v(42.27, 8.89) * mm, v(43.55, 10.7) * mm, v(44.5, 11.82) * mm], "startDerivative": vector(2.58, 4.79) * mm, "endDerivative": vector(4.86, 5.45) * mm});
            skFitSpline(sketch, "E149", {"points": [v(44.5, 11.82) * mm, v(43.09, 13.34) * mm, v(42.31, 15.08) * mm, v(41.7, 16.89) * mm], "startDerivative": vector(-4.58, 4.2) * mm, "endDerivative": vector(-1.84, 5.5) * mm});
            skFitSpline(sketch, "E150", {"points": [v(41.7, 16.89) * mm, v(44.26, 19.19) * mm], "startDerivative": vector(2.56, 2.3) * mm, "endDerivative": vector(2.56, 2.3) * mm});
            skFitSpline(sketch, "E151", {"points": [v(44.26, 19.19) * mm, v(43.04, 20.08) * mm, v(41.7, 21.47) * mm, v(40.6, 22.97) * mm], "startDerivative": vector(-3.91, 2.63) * mm, "endDerivative": vector(-2.68, 4.5) * mm});
            skFitSpline(sketch, "E152", {"points": [v(40.6, 22.97) * mm, v(39.56, 22.97) * mm, v(38.04, 23.18) * mm, v(36.56, 23.49) * mm], "startDerivative": vector(-3.66, -0.13) * mm, "endDerivative": vector(-4.21, 0.9) * mm});
            skFitSpline(sketch, "E153", {"points": [v(36.56, 23.49) * mm, v(36.56, 22.57) * mm, v(36.23, 20.6) * mm, v(35.69, 18.34) * mm], "startDerivative": vector(0.17, -3.37) * mm, "endDerivative": vector(-1.44, -5.72) * mm});
            skFitSpline(sketch, "E154", {"points": [v(35.69, 18.34) * mm, v(36.56, 16.89) * mm, v(37.7, 15.42) * mm, v(38.58, 14.4) * mm, v(40.6, 13.24) * mm], "startDerivative": vector(3.26, -6.03) * mm, "endDerivative": vector(8.43, -4) * mm});
            skFitSpline(sketch, "E155", {"points": [v(40.6, 13.24) * mm, v(38.98, 6.69) * mm], "startDerivative": vector(-1.62, -6.55) * mm, "endDerivative": vector(-1.62, -6.55) * mm});
            skFitSpline(sketch, "E156", {"points": [v(38.98, 6.69) * mm, v(38.18, 6.69) * mm, v(36.76, 6.95) * mm, v(35.93, 7.2) * mm], "startDerivative": vector(-2.45, -0.14) * mm, "endDerivative": vector(-2.45, 0.83) * mm});
            skFitSpline(sketch, "E157", {"points": [v(35.93, 7.2) * mm, v(34.73, 4.66) * mm], "startDerivative": vector(-1.2, -2.54) * mm, "endDerivative": vector(-1.2, -2.54) * mm});
            skFitSpline(sketch, "E158", {"points": [v(51.06, 4.62) * mm, v(51.87, 4.62) * mm], "startDerivative": vector(0.81, 0) * mm, "endDerivative": vector(0.81, 0) * mm});
            skFitSpline(sketch, "E159", {"points": [v(51.87, 4.62) * mm, v(52.78, 6.08) * mm], "startDerivative": vector(0.9, 1.46) * mm, "endDerivative": vector(0.9, 1.46) * mm});
            skFitSpline(sketch, "E160", {"points": [v(52.78, 6.08) * mm, v(53.45, 4.62) * mm], "startDerivative": vector(0.67, -1.46) * mm, "endDerivative": vector(0.67, -1.46) * mm});
            skFitSpline(sketch, "E161", {"points": [v(53.45, 4.62) * mm, v(56.76, 4.62) * mm], "startDerivative": vector(3.31, 0) * mm, "endDerivative": vector(3.31, 0) * mm});
            skFitSpline(sketch, "E162", {"points": [v(56.76, 4.62) * mm, v(56.97, 5.19) * mm, v(57.12, 5.91) * mm, v(57.49, 7.28) * mm, v(57.6, 9.57) * mm, v(57.2, 12.4) * mm, v(56.76, 13.97) * mm], "startDerivative": vector(2.24, 5.2) * mm, "endDerivative": vector(-2.63, 8.2) * mm});
            skFitSpline(sketch, "E163", {"points": [v(56.76, 13.97) * mm, v(57.66, 14.73) * mm, v(58.62, 15.7) * mm], "startDerivative": vector(1.89, 1.48) * mm, "endDerivative": vector(1.82, 1.96) * mm});
            skFitSpline(sketch, "E164", {"points": [v(58.62, 15.7) * mm, v(57.66, 16.82) * mm, v(56.76, 18.25) * mm, v(56.09, 19.28) * mm, v(55.4, 20.57) * mm, v(54.79, 21.86) * mm, v(54.39, 22.84) * mm, v(54.04, 24.31) * mm, v(53.85, 25.85) * mm, v(53.8, 27.13) * mm, v(53.78, 28.84) * mm, v(53.94, 30.26) * mm], "startDerivative": vector(-10.63, 11.18) * mm, "endDerivative": vector(3.2, 15.06) * mm});
            skFitSpline(sketch, "E165", {"points": [v(53.94, 30.26) * mm, v(53.35, 29.75) * mm, v(52.56, 28.93) * mm, v(51.9, 27.62) * mm, v(51.6, 26.72) * mm, v(51.42, 26.14) * mm, v(51.4, 25.66) * mm], "startDerivative": vector(-3.52, -3.08) * mm, "endDerivative": vector(-0.07, -3.33) * mm});
            skFitSpline(sketch, "E166", {"points": [v(51.4, 25.66) * mm, v(50.3, 26.21) * mm, v(49.4, 26.8) * mm, v(48.05, 28.08) * mm, v(47, 29.36) * mm, v(46.29, 30.48) * mm, v(45.85, 31.48) * mm], "startDerivative": vector(-7.2, 3.5) * mm, "endDerivative": vector(-2.63, 6.7) * mm});
            skFitSpline(sketch, "E167", {"points": [v(45.85, 31.48) * mm, v(45.57, 30.76) * mm, v(45.25, 29.6) * mm, v(45.19, 28.67) * mm, v(45.27, 27.6) * mm, v(45.5, 26.73) * mm, v(45.85, 25.74) * mm, v(46.21, 25.04) * mm], "startDerivative": vector(-2.16, -5.1) * mm, "endDerivative": vector(2.9, -4.63) * mm});
            skFitSpline(sketch, "E168", {"points": [v(46.21, 25.04) * mm, v(45.3, 25.27) * mm, v(43.95, 25.68) * mm, v(42.21, 26.31) * mm, v(41.05, 26.77) * mm, v(39.73, 27.39) * mm], "startDerivative": vector(-5.3, 1.21) * mm, "endDerivative": vector(-6.61, 3.2) * mm});
            skFitSpline(sketch, "E169", {"points": [v(39.73, 27.39) * mm, v(40.04, 26.76) * mm, v(40.34, 26.21) * mm, v(40.8, 25.46) * mm, v(41.33, 24.63) * mm, v(42.38, 23.23) * mm, v(43.59, 21.99) * mm, v(44.98, 20.62) * mm, v(46.21, 19.6) * mm, v(47.68, 18.6) * mm, v(49.4, 17.76) * mm, v(51.3, 17.05) * mm, v(52.66, 16.68) * mm, v(52.64, 16.68) * mm], "startDerivative": vector(5.48, -11.1) * mm, "endDerivative": vector(-2.87, 0.22) * mm});
            skFitSpline(sketch, "E170", {"points": [v(52.66, 16.68) * mm, v(52.95, 15.94) * mm, v(53.64, 14.1) * mm, v(54.1, 12.56) * mm, v(54.44, 11.22) * mm, v(54.67, 10) * mm, v(54.76, 8.46) * mm, v(54.79, 6.73) * mm], "startDerivative": vector(2.37, -6.08) * mm, "endDerivative": vector(0.13, -11.11) * mm});
            skFitSpline(sketch, "E171", {"points": [v(54.79, 6.73) * mm, v(54.14, 6.85) * mm, v(53.32, 6.98) * mm, v(52.41, 7.18) * mm, v(52.07, 7.32) * mm], "startDerivative": vector(-2.59, 0.48) * mm, "endDerivative": vector(-1.6, 0.74) * mm});
            skFitSpline(sketch, "E172", {"points": [v(52.07, 7.32) * mm, v(51.06, 4.62) * mm], "startDerivative": vector(-1, -2.7) * mm, "endDerivative": vector(-1, -2.7) * mm});
            skSolve(sketch);
        }
        {
            var Q0;
            Q0 = qSketchRegion(id + "F4", true);
            extrude(context, id + "F5", {"entities" : qUnion([Q0]), "operationType" : NewBodyOperationType.REMOVE, "oppositeDirection" : true, "depth" : 1 * mm, "offsetDistance" : 25 * mm});
        }
    });
